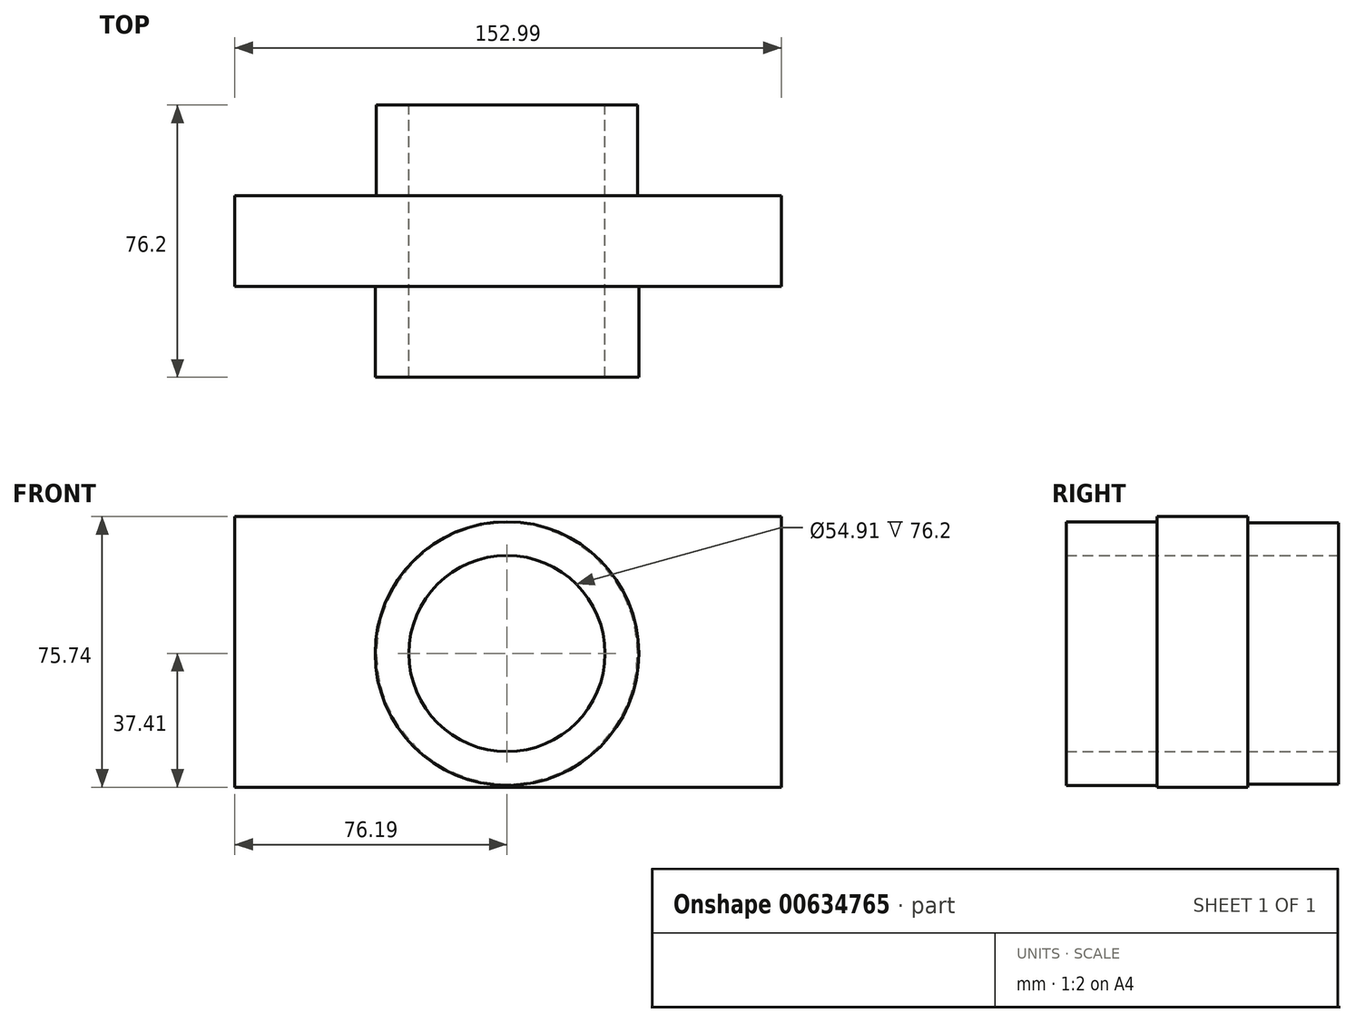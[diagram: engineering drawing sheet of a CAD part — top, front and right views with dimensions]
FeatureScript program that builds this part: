
annotation { "Feature Type Name" : "Feature", "Feature Type Description" : "" }
export const myFeature = defineFeature(function(context is Context, id is Id, definition is map)
    precondition{}
    {
        {
            var Q0;
            Q0=qCreatedBy(makeId("Front.planeOp"),FACE);
            var sketch = newSketch(context, id + "F0", { "sketchPlane" : qUnion([Q0])});
            skLineSegment(sketch, "E0.bottom", {"start": v(-76.2, 38.33) * mm, "end": v(76.8, 38.33) * mm});
            skLineSegment(sketch, "E0.top", {"start": v(-76.2, -37.4) * mm, "end": v(76.8, -37.4) * mm});
            skLineSegment(sketch, "E0.left", {"start": v(-76.2, 38.33) * mm, "end": v(-76.2, -37.4) * mm});
            skLineSegment(sketch, "E0.right", {"start": v(76.8, 38.33) * mm, "end": v(76.8, -37.4) * mm});
            skSolve(sketch);
        }
        {
            var Q0;
            Q0 = qSketchRegion(id + "F0", true);
            extrude(context, id + "F1", {"entities" : qUnion([Q0]), "depth" : 25.4 * mm, "offsetDistance" : 25.4 * mm});
        }
        {
            var Q0;
            Q0=makeQuery(id+"F1.opExtrude","CAP_FACE",FACE,{"disambiguationData":[OSD([sQuery(id+"F0.wireOp",EDGE,"E0.bottom"),sQuery(id+"F0.wireOp",EDGE,"E0.top"),sQuery(id+"F0.wireOp",EDGE,"E0.left"),sQuery(id+"F0.wireOp",EDGE,"E0.right")])],"isStart":false});
            var sketch = newSketch(context, id + "F2", { "sketchPlane" : qUnion([Q0])});
            skCircle(sketch, "E1", {"center": v(0, 0) * mm, "radius": 36.9 * mm});
            skSolve(sketch);
        }
        {
            var Q0;
            Q0 = qSketchRegion(id + "F2", true);
            extrude(context, id + "F3", {"entities" : qUnion([Q0]), "operationType" : NewBodyOperationType.ADD, "depth" : 25.4 * mm, "offsetDistance" : 25.4 * mm});
        }
        {
            var Q0;
            Q0=makeQuery(id+"F1.opExtrude","CAP_FACE",FACE,{"disambiguationData":[OSD([sQuery(id+"F0.wireOp",EDGE,"E0.bottom"),sQuery(id+"F0.wireOp",EDGE,"E0.top"),sQuery(id+"F0.wireOp",EDGE,"E0.left"),sQuery(id+"F0.wireOp",EDGE,"E0.right")])],"isStart":true});
            var sketch = newSketch(context, id + "F4", { "sketchPlane" : qUnion([Q0])});
            skCircle(sketch, "E2", {"center": v(0, 0) * mm, "radius": 36.55 * mm});
            skSolve(sketch);
        }
        {
            var Q0;
            Q0 = qSketchRegion(id + "F4", true);
            extrude(context, id + "F5", {"entities" : qUnion([Q0]), "operationType" : NewBodyOperationType.ADD, "depth" : 25.4 * mm, "offsetDistance" : 25.4 * mm});
        }
        {
            var Q0;
            Q0=makeQuery(id+"F3.opExtrude","CAP_FACE",FACE,{"disambiguationData":[OSD([sQuery(id+"F2.wireOp",EDGE,"E1")])],"isStart":false});
            var sketch = newSketch(context, id + "F6", { "sketchPlane" : qUnion([Q0])});
            skCircle(sketch, "E3", {"center": v(0, 0) * mm, "radius": 25.93 * mm});
            skSolve(sketch);
        }
        {
            var Q0;
            Q0 = qSketchRegion(id + "F6", true);
            extrude(context, id + "F7", {"entities" : qUnion([Q0]), "operationType" : NewBodyOperationType.REMOVE, "oppositeDirection" : true, "depth" : 25.4 * mm, "offsetDistance" : 25.4 * mm});
        }
        {
            var Q0;
            Q0=makeQuery(id+"F5.opExtrude","CAP_FACE",FACE,{"disambiguationData":[OSD([sQuery(id+"F4.wireOp",EDGE,"E2")])],"isStart":false});
            var sketch = newSketch(context, id + "F8", { "sketchPlane" : qUnion([Q0])});
            skCircle(sketch, "E4", {"center": v(0, 0) * mm, "radius": 27.45 * mm});
            skSolve(sketch);
        }
        {
            var Q0;
            Q0 = qSketchRegion(id + "F8", true);
            extrude(context, id + "F9", {"entities" : qUnion([Q0]), "operationType" : NewBodyOperationType.REMOVE, "oppositeDirection" : true, "depth" : 83.31 * mm, "offsetDistance" : 25.4 * mm});
        }
    });
